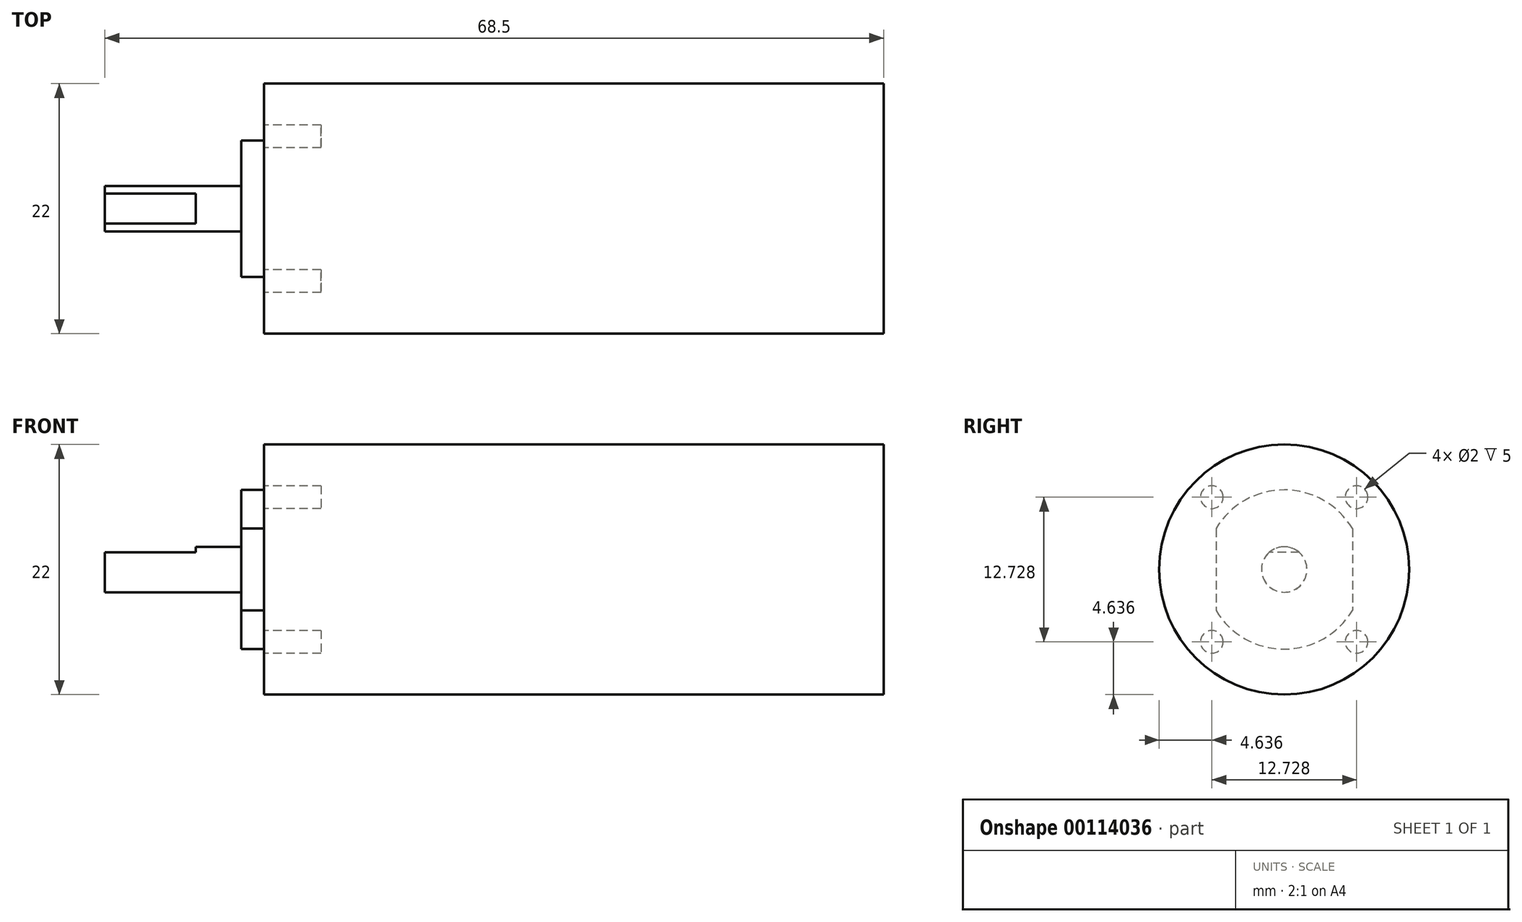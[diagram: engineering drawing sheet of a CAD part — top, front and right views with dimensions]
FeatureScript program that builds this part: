
annotation { "Feature Type Name" : "Feature", "Feature Type Description" : "" }
export const myFeature = defineFeature(function(context is Context, id is Id, definition is map)
    precondition{}
    {
        {
            var Q0;
            Q0=qCreatedBy(makeId("Right.planeOp"),FACE);
            var sketch = newSketch(context, id + "F0", { "sketchPlane" : qUnion([Q0])});
            skCircle(sketch, "E0", {"center": v(0, 0) * mm, "radius": 11 * mm});
            skSolve(sketch);
        }
        {
            var Q0;
            Q0 = qSketchRegion(id + "F0", true);
            extrude(context, id + "F1", {"entities" : qUnion([Q0]), "depth" : 54.5 * mm});
        }
        {
            var Q0;
            Q0=makeQuery(id+"F1.opExtrude","CAP_FACE",FACE,{"disambiguationData":[OSD([sQuery(id+"F0.wireOp",EDGE,"E0")])],"isStart":true});
            var sketch = newSketch(context, id + "F2", { "sketchPlane" : qUnion([Q0])});
            skArc(sketch, "E1", {"start": v(-6, -3.6) * mm, "mid": v(0, -7) * mm, "end": v(6, -3.6) * mm});
            skLineSegment(sketch, "E2", {"start": v(-6, 3.6) * mm, "end": v(-6, -3.6) * mm});
            skLineSegment(sketch, "E3", {"start": v(6, 3.6) * mm, "end": v(6, -3.6) * mm});
            skArc(sketch, "E4.trimOffspring", {"start": v(6, 3.6) * mm, "mid": v(0, 7) * mm, "end": v(-6, 3.6) * mm});
            skSolve(sketch);
        }
        {
            var Q0;
            Q0 = qSketchRegion(id + "F2", true);
            extrude(context, id + "F3", {"entities" : qUnion([Q0]), "operationType" : NewBodyOperationType.ADD, "depth" : 2 * mm});
        }
        {
            var Q0;
            Q0=makeQuery(id+"F3.opExtrude","CAP_FACE",FACE,{"disambiguationData":[OSD([sQuery(id+"F2.wireOp",EDGE,"E1"),sQuery(id+"F2.wireOp",EDGE,"E2"),sQuery(id+"F2.wireOp",EDGE,"E3"),sQuery(id+"F2.wireOp",EDGE,"E4.trimOffspring")])],"isStart":false});
            var sketch = newSketch(context, id + "F4", { "sketchPlane" : qUnion([Q0])});
            skCircle(sketch, "E5", {"center": v(0, 0) * mm, "radius": 2 * mm});
            skSolve(sketch);
        }
        {
            var Q0;
            Q0=makeQuery(id+"F4.imprint","IMPRINT",FACE,{"disambiguationData":[TD([[makeQuery(id+"F4.imprint","IMPRINT",EDGE,{"derivedFrom":sQuery(id+"F4.wireOp",EDGE,"E5")}),1.0]])]});
            extrude(context, id + "F5", {"entities" : qUnion([Q0]), "operationType" : NewBodyOperationType.ADD, "depth" : 12 * mm});
        }
        {
            var Q0;
            Q0=makeQuery(id+"F5.opExtrude","CAP_FACE",FACE,{"disambiguationData":[OSD([sQuery(id+"F4.wireOp",EDGE,"E5")])],"isStart":false});
            var sketch = newSketch(context, id + "F6", { "sketchPlane" : qUnion([Q0])});
            skPoint(sketch, "E6.center.orphan", {"position": v(0, 0) * mm});
            skLineSegment(sketch, "E7", {"start": v(-1.32, 1.5) * mm, "end": v(1.32, 1.5) * mm});
            skLineSegment(sketch, "E8", {"start": v(-1.32, 1.5) * mm, "end": v(-1.32, 2.42) * mm});
            skLineSegment(sketch, "E9", {"start": v(-1.32, 2.42) * mm, "end": v(1.82, 2.42) * mm});
            skLineSegment(sketch, "E10", {"start": v(1.82, 2.42) * mm, "end": v(1.32, 1.5) * mm});
            skSolve(sketch);
        }
        {
            var Q0;
            Q0 = qSketchRegion(id + "F6", true);
            extrude(context, id + "F7", {"entities" : qUnion([Q0]), "operationType" : NewBodyOperationType.REMOVE, "oppositeDirection" : true, "depth" : 8 * mm});
        }
        {
            var Q0;
            Q0=makeQuery(id+"F1.opExtrude","CAP_FACE",FACE,{"disambiguationData":[OSD([sQuery(id+"F0.wireOp",EDGE,"E0")])],"isStart":true});
            var sketch = newSketch(context, id + "F8", { "sketchPlane" : qUnion([Q0])});
            skCircle(sketch, "E11", {"center": v(0, 0) * mm, "radius": 9 * mm, "construction": true});
            skCircle(sketch, "E12", {"center": v(6.36, 6.36) * mm, "radius": 1 * mm});
            skCircle(sketch, "E13.1.0", {"center": v(6.36, -6.36) * mm, "radius": 1 * mm});
            skCircle(sketch, "E13.2.0", {"center": v(-6.36, -6.36) * mm, "radius": 1 * mm});
            skCircle(sketch, "E13.3.0", {"center": v(-6.36, 6.36) * mm, "radius": 1 * mm});
            skLineSegment(sketch, "E13.anchor1", {"start": v(0, 0) * mm, "end": v(6.36, 6.36) * mm, "construction": true});
            skLineSegment(sketch, "E13.anchor2", {"start": v(0, 0) * mm, "end": v(-6.36, 6.36) * mm, "construction": true});
            skSolve(sketch);
        }
        {
            var Q0;
            Q0 = qSketchRegion(id + "F8", true);
            extrude(context, id + "F9", {"entities" : qUnion([Q0]), "operationType" : NewBodyOperationType.REMOVE, "oppositeDirection" : true, "depth" : 5 * mm});
        }
    });
